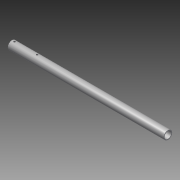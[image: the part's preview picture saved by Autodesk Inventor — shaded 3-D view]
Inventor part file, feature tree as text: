
AUTODESK INVENTOR PART (.ipt)
format: ipt  version: 2014 (Build 180170000, 170)  size: 124,416 bytes
history: native  units: in
note: dims shown in document units (in); Inventor stores cm internally (conversion verified against a paired STEP export)
features: other x2, extrude x2, sketch x2, plane x1, imported_body x1, projected_geometry x1
ambient origin geometry x8: Origin, YZ Plane, XZ Plane, XY Plane, X Axis, Y Axis, Z Axis, Center Point
bodies: Body1 (feature_tree)
feature tree (9):
  parser-record x1  (decoder bookkeeping rows leaked as tree rows — omitted from the tree; the rows remain in map.json)
  other  "4347K3111"
  extrude  "Extrusion1"  Depth=0.19in
  plane  "Work Plane1"
  extrude  "Extrusion2"  Depth=2.5in
  imported_body  "Base1"
  sketch  "Sketch1"  dims[d0=3.5in d1=0.0in d2=0.19in]
  sketch  "Sketch2"  dims[d3=0.25in d4=2.5in d5=1.0in d6=0.0in]
  projected_geometry  "Projected Loop1"
